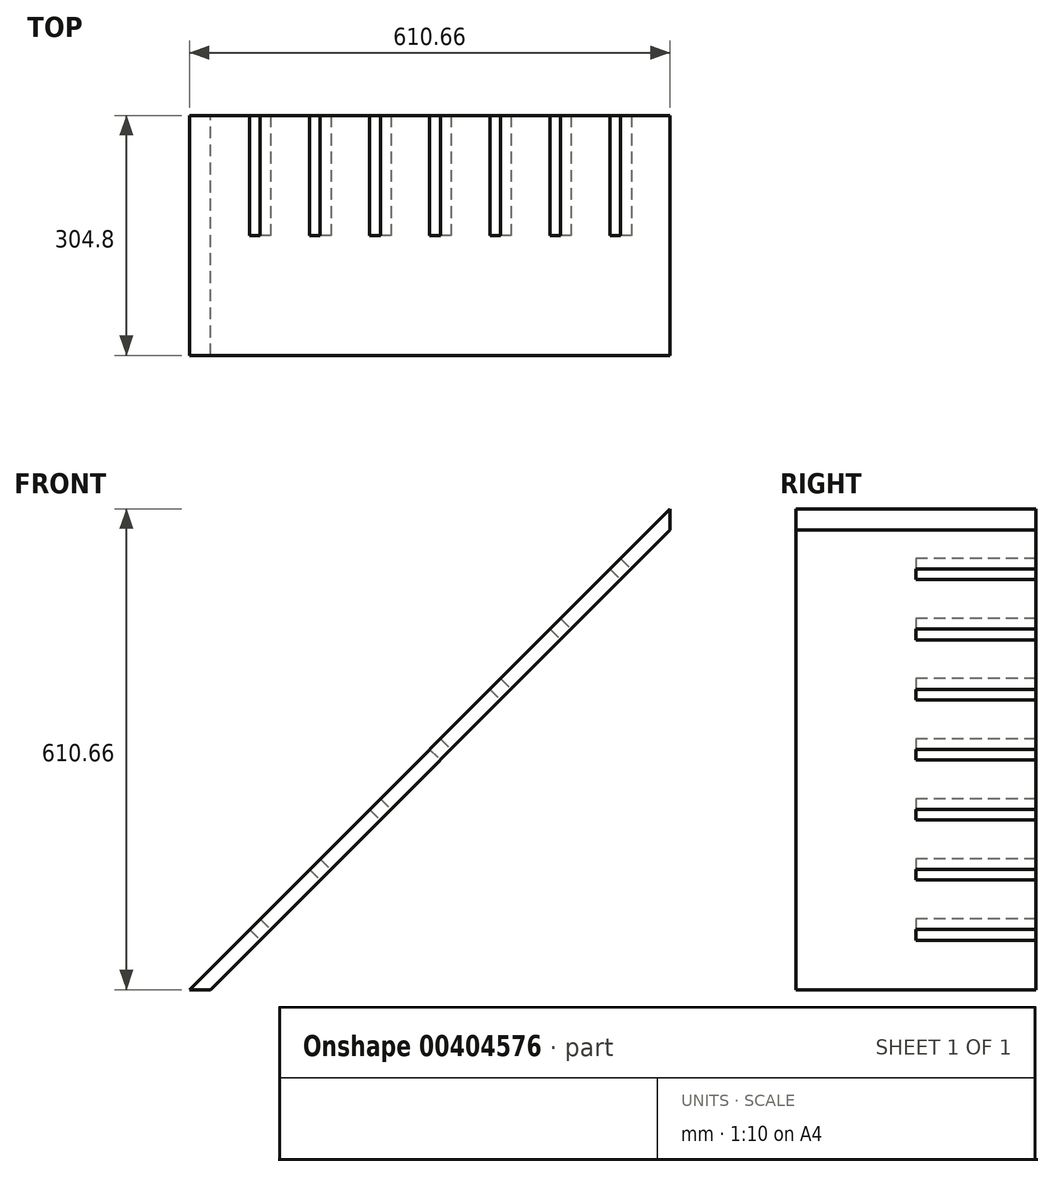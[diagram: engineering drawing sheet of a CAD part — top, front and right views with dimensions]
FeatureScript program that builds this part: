
annotation { "Feature Type Name" : "Feature", "Feature Type Description" : "" }
export const myFeature = defineFeature(function(context is Context, id is Id, definition is map)
    precondition{}
    {
        {
            var Q0;
            Q0=qCreatedBy(makeId("Front.planeOp"),FACE);
            var sketch = newSketch(context, id + "F0", { "sketchPlane" : qUnion([Q0])});
            skLineSegment(sketch, "E0", {"start": v(-337.22, 0) * mm, "end": v(273.44, 610.66) * mm});
            skPoint(sketch, "E1.MirrorP", {"position": v(53.93, 355.6) * mm});
            skLineSegment(sketch, "E2.MirrorCS", {"start": v(-310.28, 0) * mm, "end": v(273.44, 583.72) * mm});
            skLineSegment(sketch, "E3", {"start": v(273.44, 583.72) * mm, "end": v(273.44, 610.66) * mm});
            skLineSegment(sketch, "E4", {"start": v(-310.28, 0) * mm, "end": v(-337.22, 0) * mm});
            skSolve(sketch);
        }
        {
            var Q0;
            Q0=qSketchRegion(id+"F0",true);
            extrude(context, id + "F1", {"entities" : qUnion([Q0]), "endBound" : BoundingType.SYMMETRIC, "depth" : 304.8 * mm});
        }
        {
            var Q0;
            Q0=makeQuery(id+"F1.opExtrude","SWEPT_FACE",FACE,{"disambiguationData":[OSD([sQuery(id+"F0.wireOp",EDGE,"E2.MirrorCS")])]});
            var sketch = newSketch(context, id + "F2", { "sketchPlane" : qUnion([Q0])});
            skLineSegment(sketch, "E5.bottom", {"start": v(152.4, 536.25) * mm, "end": v(0, 536.25) * mm});
            skLineSegment(sketch, "E5.top", {"start": v(152.4, 517.2) * mm, "end": v(0, 517.2) * mm});
            skLineSegment(sketch, "E5.left", {"start": v(152.4, 536.25) * mm, "end": v(152.4, 517.2) * mm});
            skLineSegment(sketch, "E5.right", {"start": v(0, 536.25) * mm, "end": v(0, 517.2) * mm});
            skLineSegment(sketch, "E6.bottom", {"start": v(152.4, 428.3) * mm, "end": v(0, 428.3) * mm});
            skLineSegment(sketch, "E6.top", {"start": v(152.4, 409.25) * mm, "end": v(0, 409.25) * mm});
            skLineSegment(sketch, "E6.left", {"start": v(152.4, 428.3) * mm, "end": v(152.4, 409.25) * mm});
            skLineSegment(sketch, "E6.right", {"start": v(0, 428.3) * mm, "end": v(0, 409.25) * mm});
            skLineSegment(sketch, "E7.bottom", {"start": v(152.4, 320.35) * mm, "end": v(0, 320.35) * mm});
            skLineSegment(sketch, "E7.top", {"start": v(152.4, 301.3) * mm, "end": v(0, 301.3) * mm});
            skLineSegment(sketch, "E7.left", {"start": v(152.4, 320.35) * mm, "end": v(152.4, 301.3) * mm});
            skLineSegment(sketch, "E7.right", {"start": v(0, 320.35) * mm, "end": v(0, 301.3) * mm});
            skLineSegment(sketch, "E8.bottom", {"start": v(152.4, 212.4) * mm, "end": v(0, 212.4) * mm});
            skLineSegment(sketch, "E8.top", {"start": v(152.4, 193.35) * mm, "end": v(0, 193.35) * mm});
            skLineSegment(sketch, "E8.left", {"start": v(152.4, 212.4) * mm, "end": v(152.4, 193.35) * mm});
            skLineSegment(sketch, "E8.right", {"start": v(0, 212.4) * mm, "end": v(0, 193.35) * mm});
            skLineSegment(sketch, "E9.bottom", {"start": v(152.4, 104.45) * mm, "end": v(0, 104.45) * mm});
            skLineSegment(sketch, "E9.top", {"start": v(152.4, 85.4) * mm, "end": v(0, 85.4) * mm});
            skLineSegment(sketch, "E9.left", {"start": v(152.4, 104.45) * mm, "end": v(152.4, 85.4) * mm});
            skLineSegment(sketch, "E9.right", {"start": v(0, 104.45) * mm, "end": v(0, 85.4) * mm});
            skLineSegment(sketch, "E10.bottom", {"start": v(152.4, -3.5) * mm, "end": v(0, -3.5) * mm});
            skLineSegment(sketch, "E10.top", {"start": v(152.4, -22.55) * mm, "end": v(0, -22.55) * mm});
            skLineSegment(sketch, "E10.left", {"start": v(152.4, -3.5) * mm, "end": v(152.4, -22.55) * mm});
            skLineSegment(sketch, "E10.right", {"start": v(0, -3.5) * mm, "end": v(0, -22.55) * mm});
            skLineSegment(sketch, "E11.bottom", {"start": v(152.4, -111.45) * mm, "end": v(0, -111.45) * mm});
            skLineSegment(sketch, "E11.top", {"start": v(152.4, -130.5) * mm, "end": v(0, -130.5) * mm});
            skLineSegment(sketch, "E11.left", {"start": v(152.4, -111.45) * mm, "end": v(152.4, -130.5) * mm});
            skLineSegment(sketch, "E11.right", {"start": v(0, -111.45) * mm, "end": v(0, -130.5) * mm});
            skSolve(sketch);
        }
        {
            var Q0;
            Q0 = qSketchRegion(id + "F2", true);
            extrude(context, id + "F3", {"entities" : qUnion([Q0]), "operationType" : NewBodyOperationType.REMOVE, "oppositeDirection" : true, "depth" : 19.05 * mm});
        }
    });
